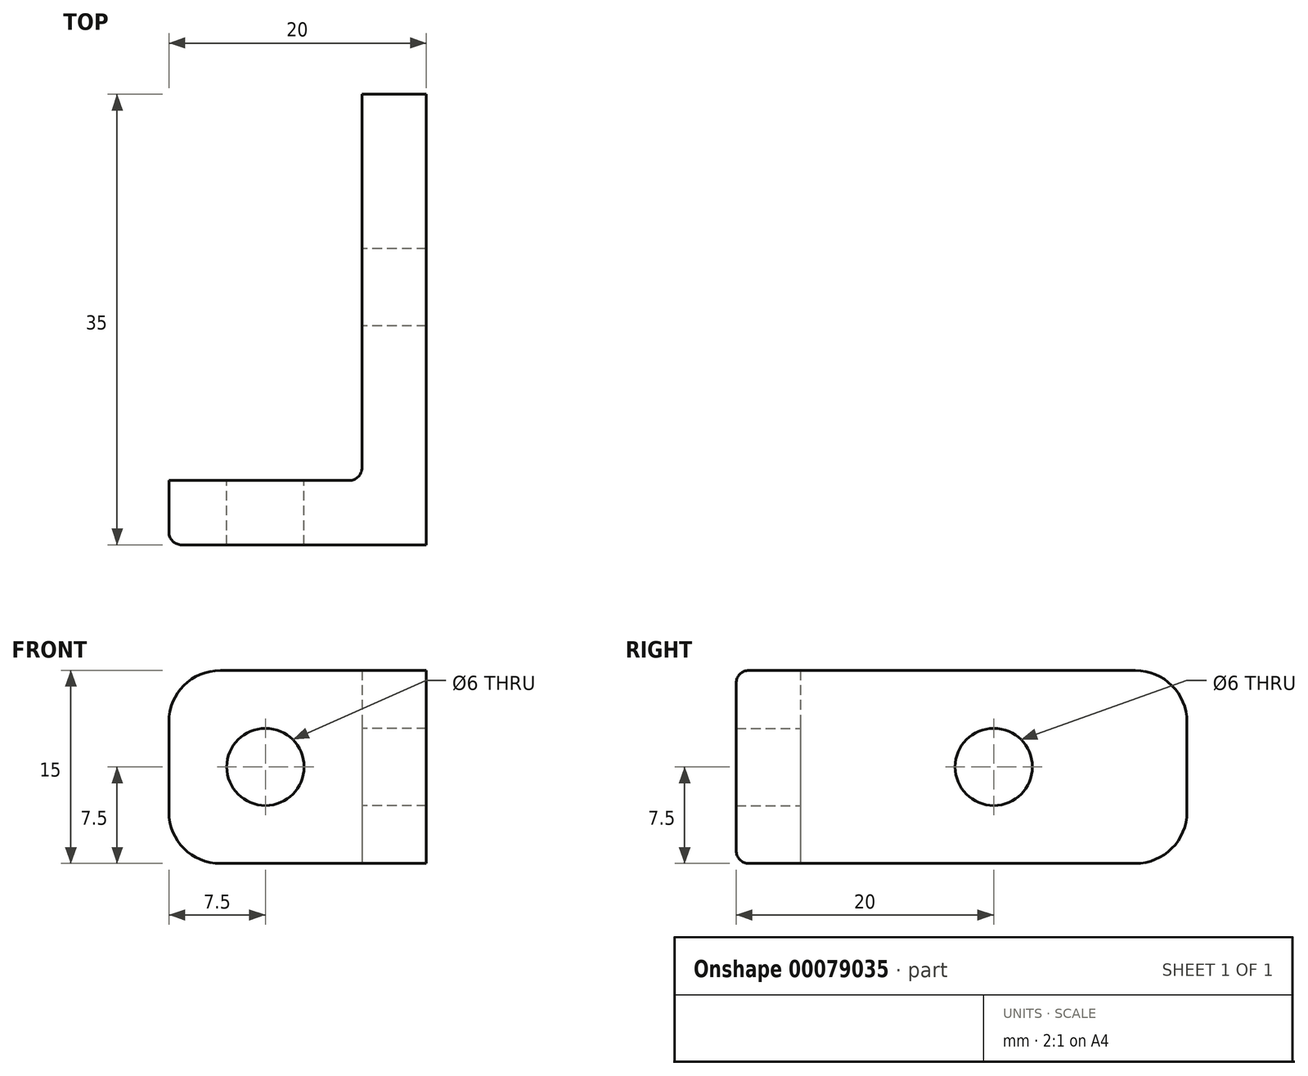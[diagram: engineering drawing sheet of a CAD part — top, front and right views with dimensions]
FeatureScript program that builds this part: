
annotation { "Feature Type Name" : "Feature", "Feature Type Description" : "" }
export const myFeature = defineFeature(function(context is Context, id is Id, definition is map)
    precondition{}
    {
        {
            var Q0;
            Q0=qCreatedBy(makeId("Top.planeOp"),FACE);
            var sketch = newSketch(context, id + "F4", { "sketchPlane" : qUnion([Q0])});
            skLineSegment(sketch, "E0.bottom", {"start": v(2.5, -17.5) * mm, "end": v(-2.5, -17.5) * mm});
            skLineSegment(sketch, "E0.top", {"start": v(2.5, 17.5) * mm, "end": v(-2.5, 17.5) * mm});
            skLineSegment(sketch, "E0.left", {"start": v(2.5, -17.5) * mm, "end": v(2.5, 17.5) * mm});
            skLineSegment(sketch, "E0.right", {"start": v(-2.5, -12.5) * mm, "end": v(-2.5, 17.5) * mm});
            skPoint(sketch, "E0.middle", {"position": v(0, 0) * mm});
            skLineSegment(sketch, "E1.bottom", {"start": v(2.5, -17.5) * mm, "end": v(-17.5, -17.5) * mm});
            skLineSegment(sketch, "E1.top", {"start": v(-2.5, -12.5) * mm, "end": v(-17.5, -12.5) * mm});
            skLineSegment(sketch, "E1.left", {"start": v(2.5, -17.5) * mm, "end": v(2.5, -12.5) * mm});
            skLineSegment(sketch, "E1.right", {"start": v(-17.5, -17.5) * mm, "end": v(-17.5, -12.5) * mm});
            skSolve(sketch);
        }
        {
            var Q0;
            Q0=makeQuery(id+"F4.imprint","IMPRINT",FACE,{"disambiguationData":[TD([[makeQuery(id+"F4.imprint","IMPRINT",EDGE,{"derivedFrom":sQuery(id+"F4.wireOp",EDGE,"E0.top")}),1.0]])]});
            extrude(context, id + "F5", {"entities" : qUnion([Q0]), "depth" : 15 * mm});
        }
        {
            var Q0;
            Q0=makeQuery(id+"F5.opExtrude","SWEPT_FACE",FACE,{"disambiguationData":[OSD([sQuery(id+"F4.wireOp",EDGE,"E1.top")])]});
            var sketch = newSketch(context, id + "F6", { "sketchPlane" : qUnion([Q0])});
            skPoint(sketch, "E2", {"position": v(10, 7.5) * mm});
            skCircle(sketch, "E3", {"center": v(10, 7.5) * mm, "radius": 3 * mm});
            skSolve(sketch);
        }
        {
            var Q0;
            Q0=makeQuery(id+"F5.opExtrude","SWEPT_FACE",FACE,{"disambiguationData":[OSD([sQuery(id+"F4.wireOp",EDGE,"E0.right")])]});
            var sketch = newSketch(context, id + "F0", { "sketchPlane" : qUnion([Q0])});
            skPoint(sketch, "E4", {"position": v(-2.5, 7.5) * mm});
            skCircle(sketch, "E5", {"center": v(-2.5, 7.5) * mm, "radius": 3 * mm});
            skSolve(sketch);
        }
        {
            var Q0;
            Q0=makeQuery(id+"F0.imprint","IMPRINT",FACE,{"disambiguationData":[TD([[makeQuery(id+"F0.imprint","IMPRINT",EDGE,{"derivedFrom":sQuery(id+"F0.wireOp",EDGE,"E5")}),1.0]])]});
            extrude(context, id + "F1", {"entities" : qUnion([Q0]), "operationType" : NewBodyOperationType.REMOVE, "oppositeDirection" : true, "depth" : 5 * mm});
        }
        {
            var Q0;
            Q0=makeQuery(id+"F5.opExtrude","CAP_EDGE",EDGE,{"disambiguationData":[OSD([sQuery(id+"F4.wireOp",EDGE,"E0.top")])],"isStart":false});
            var Q1;
            Q1=makeQuery(id+"F5.opExtrude","CAP_EDGE",EDGE,{"disambiguationData":[OSD([sQuery(id+"F4.wireOp",EDGE,"E0.top")])],"isStart":true});
            var Q2;
            Q2=makeQuery(id+"F5.opExtrude","CAP_EDGE",EDGE,{"disambiguationData":[OSD([sQuery(id+"F4.wireOp",EDGE,"E1.right")])],"isStart":true});
            var Q3;
            Q3=makeQuery(id+"F5.opExtrude","CAP_EDGE",EDGE,{"disambiguationData":[OSD([sQuery(id+"F4.wireOp",EDGE,"E1.right")])],"isStart":false});
            fillet(context, id + "F7", {"entities" : qUnion([Q0, Q1, Q2, Q3]), "radius" : 4 * mm, "tangentPropagation" : true, "allowEdgeOverflow" : false});
        }
        {
            var Q0;
            Q0=makeQuery(id+"F5.opExtrude","SWEPT_EDGE",EDGE,{"disambiguationData":[OSD([sQuery(id+"F4.wireOp",EDGE,"E0.right"),sQuery(id+"F4.wireOp",EDGE,"E1.top")])]});
            fillet(context, id + "F8", {"entities" : qUnion([Q0]), "radius" : 1 * mm, "tangentPropagation" : true, "allowEdgeOverflow" : false});
        }
        {
            var Q0;
            Q0=makeQuery(id+"F5.opExtrude","SWEPT_EDGE",EDGE,{"disambiguationData":[OSD([sQuery(id+"F4.wireOp",EDGE,"E1.bottom"),sQuery(id+"F4.wireOp",EDGE,"E1.left")])]});
            fillet(context, id + "F2", {"entities" : qUnion([Q0]), "radius" : 1 * mm, "tangentPropagation" : true, "allowEdgeOverflow" : false});
        }
        {
            var Q0;
            Q0=sQuery(id+"F6.wireOp",VERTEX,"E2");
            var Q1;
            Q1=makeQuery(id+"F5.opExtrude","SWEPT_BODY",BODY,{"disambiguationData":[OSD([sQuery(id+"F4.wireOp",EDGE,"E0.top"),sQuery(id+"F4.wireOp",EDGE,"E0.left"),sQuery(id+"F4.wireOp",EDGE,"E0.right"),sQuery(id+"F4.wireOp",EDGE,"E1.bottom"),sQuery(id+"F4.wireOp",EDGE,"E1.top"),sQuery(id+"F4.wireOp",EDGE,"E1.left"),sQuery(id+"F4.wireOp",EDGE,"E1.right")])]});
            hole(context, id + "F3", {"style" : HoleStyle.SIMPLE, "endStyle" : HoleEndStyle.THROUGH, "holeDiameter" : 6 * mm, "locations" : qUnion([Q0]), "scope" : qUnion([Q1]), "isTappedThrough" : true});
        }
    });
